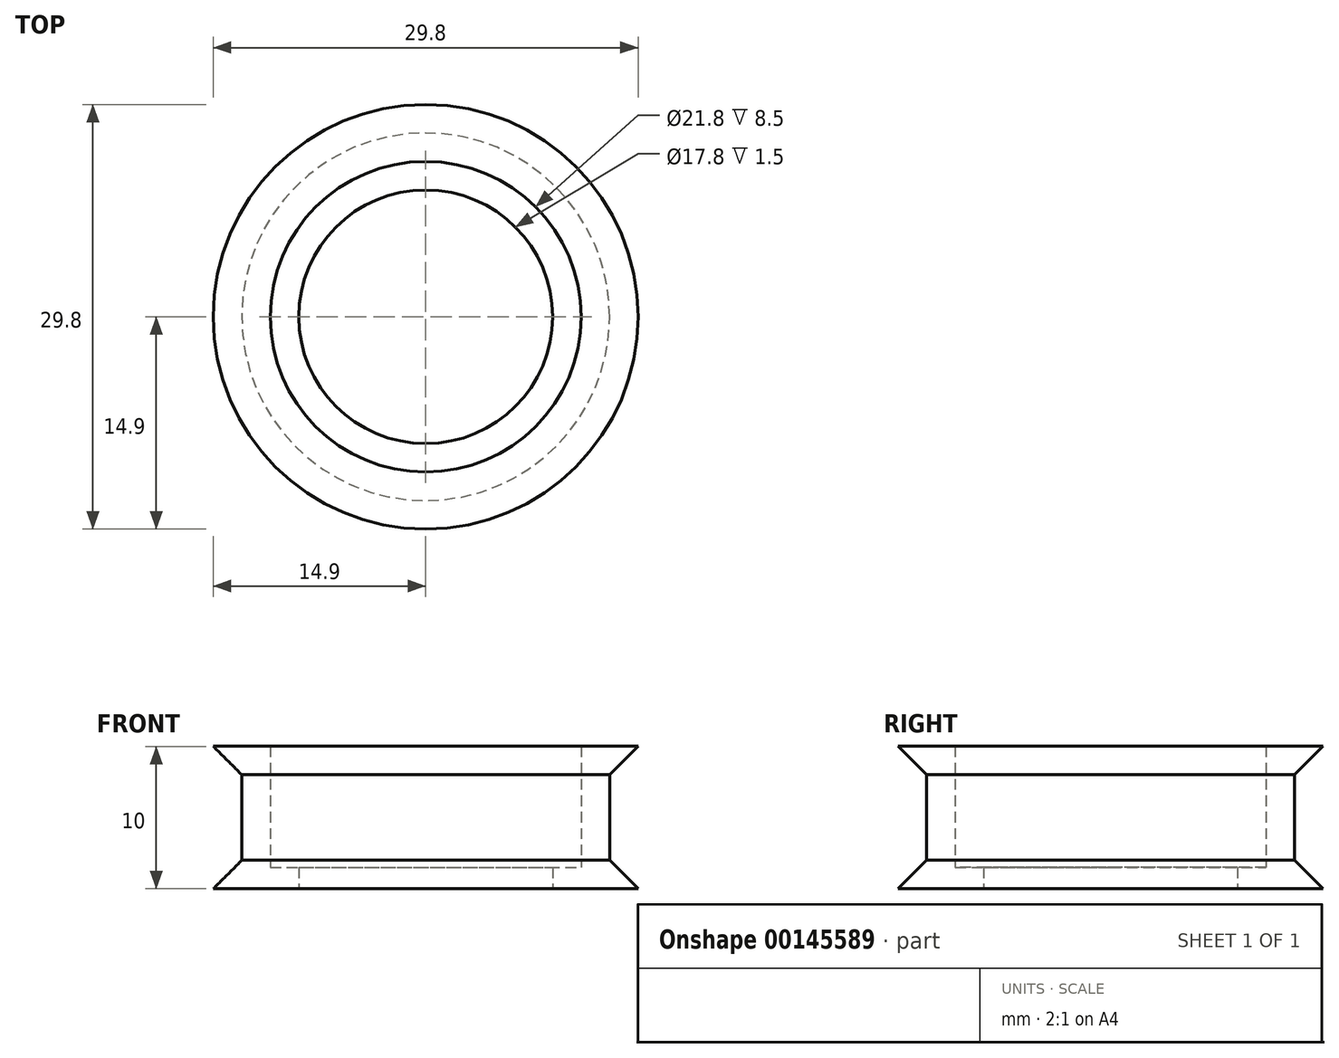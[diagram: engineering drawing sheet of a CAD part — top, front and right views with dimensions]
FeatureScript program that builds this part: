
annotation { "Feature Type Name" : "Feature", "Feature Type Description" : "" }
export const myFeature = defineFeature(function(context is Context, id is Id, definition is map)
    precondition{}
    {
        {
            var Q0;
            Q0=qCreatedBy(makeId("Front.planeOp"),FACE);
            var sketch = newSketch(context, id + "F0", { "sketchPlane" : qUnion([Q0])});
            skLineSegment(sketch, "E0", {"start": v(10.9, 4.8) * mm, "end": v(14.9, 4.8) * mm});
            skLineSegment(sketch, "E1", {"start": v(14.9, 4.8) * mm, "end": v(12.9, 2.8) * mm});
            skLineSegment(sketch, "E2", {"start": v(12.9, 2.8) * mm, "end": v(12.9, -3.2) * mm});
            skLineSegment(sketch, "E3", {"start": v(12.9, -3.2) * mm, "end": v(14.9, -5.2) * mm});
            skLineSegment(sketch, "E4", {"start": v(14.9, -5.2) * mm, "end": v(10.9, -5.2) * mm});
            skLineSegment(sketch, "E5", {"start": v(10.9, -5.2) * mm, "end": v(10.9, 4.8) * mm});
            skLineSegment(sketch, "E6", {"start": v(0, -3.77) * mm, "end": v(0, 4.95) * mm, "construction": true});
            skLineSegment(sketch, "E7.bottom", {"start": v(10.9, -5.2) * mm, "end": v(8.9, -5.2) * mm});
            skLineSegment(sketch, "E7.top", {"start": v(10.9, -3.7) * mm, "end": v(8.9, -3.7) * mm});
            skLineSegment(sketch, "E7.left", {"start": v(10.9, -5.2) * mm, "end": v(10.9, -3.7) * mm});
            skLineSegment(sketch, "E7.right", {"start": v(8.9, -5.2) * mm, "end": v(8.9, -3.7) * mm});
            skSolve(sketch);
        }
        {
            var Q0;
            Q0=qSketchRegion(id+"F0",true);
            var Q1;
            Q1=sQuery(id+"F0.wireOp",EDGE,"E6");
            revolve(context, id + "F1", {"entities" : qUnion([Q0]), "axis" : qUnion([Q1]), "revolveType" : RevolveType.FULL});
        }
    });
